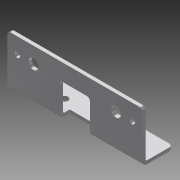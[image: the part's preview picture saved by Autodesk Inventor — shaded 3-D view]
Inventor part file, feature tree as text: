
AUTODESK INVENTOR PART (.ipt)
format: ipt  version: 2013 (Build 170138000, 138)  size: 270,336 bytes
history: native  units: in
note: dims shown in document units (in); Inventor stores cm internally (conversion verified against a paired STEP export)
features: other x7, sketch x6, sheet_metal_op x4, reference x3, chamfer x2
ambient origin geometry x8: Origin, YZ Plane, XZ Plane, XY Plane, X Axis, Y Axis, Z Axis, Center Point
bodies: Solid1 (feature_tree)
feature tree (22):
  sheet_metal_op  "Face1"
  sheet_metal_op  "Flange1"
  chamfer  "Corner Round1"
  chamfer  "Corner Round2"
  sketch  "Sketch1"  dims[d0=5.0in]
  other  "Plate1"
  sketch  "Sketch2"  dims[d1=1.125in]
  other  "Plate2"
  sheet_metal_op  "Bend1"
  sheet_metal_op  "Corner1"
  sketch  "Sketch3"  dims[d3=0.125in]
  sketch  "Sketch4"  dims[d4=0.125in]
  sketch  "Sketch5"  dims[d5=0.0625in]
  sketch  "Sketch6"  dims[d6=0.25in d7=0.125in d8=1.875in d9=90.0deg d10=0.05in d11=0.5in d12=0.125in d13=0.125in d18=1.125in d20=0.375in d21=0.0in d22=0.625in d23=0.26in d24=0.26in d25=2.0in d26=1.0in d27=0.125in d28=0.0in d29=0.125in d30=0.125in d31=0.0in d32=0.125in d33=0.0in d34=0.125in d35=0.375in d36=0.375in d37=1.25in d2=0.25in]
  reference  "Reference7"
  reference  "Reference14"
  reference  "Reference15"
  other  "Cut1"
  other  "Cut2"
  other  "Cut3"
  other  "Cut4"
  other  "Definition1"
